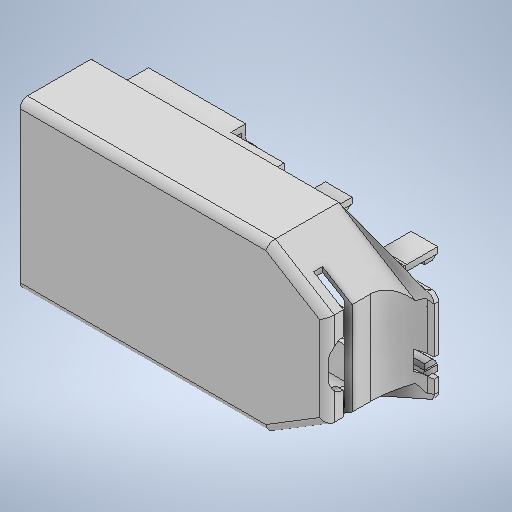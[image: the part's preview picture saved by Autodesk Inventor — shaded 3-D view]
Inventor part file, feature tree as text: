
AUTODESK INVENTOR PART (.ipt)
format: ipt  version: 2025 (Build 290162000, 162)  size: 913,408 bytes
history: native  units: mm
features: extrude x19, reference x11, fillet x7, sketch x5, other x4, plane x3, thicken_offset x2, loft x1, chamfer x1, projected_geometry x1
ambient origin geometry x8: Origin, YZ Plane, XZ Plane, XY Plane, X Axis, Y Axis, Z Axis, Center Point
bodies: Solid1 (feature_tree)
feature tree (54):
  plane  "Work Plane1"
  extrude  "Extrusion1"  Depth=0.4mm
  extrude  "Extrusion2"  Depth=0.4mm
  extrude  "Extrusion3"  Depth=0.5mm
  plane  "Work Plane2"
  loft  "Loft1"
  extrude  "Extrusion4"  Depth=2.0mm TaperAngle=0.0deg
  extrude  "Extrusion5"  Depth=2.0mm
  extrude  "Extrusion6"  Depth=2.0mm
  extrude  "Extrusion7"  Depth=2.0mm
  extrude  "Extrusion8"  Depth=2.0mm
  extrude  "Extrusion9"  Depth=2.0mm
  extrude  "Extrusion10"  TaperAngle=0.0deg  [1 undecoded]
  extrude  "Extrusion11"  TaperAngle=0.0deg  [1 undecoded]
  extrude  "Extrusion12"  Depth=2.0mm TaperAngle=0.0deg
  extrude  "Extrusion13"  Depth=10.0mm TaperAngle=0.0deg
  extrude  "Extrusion14"  Depth=2.0mm TaperAngle=0.0deg
  chamfer  "Chamfer1"  Distance=0.3mm
  thicken_offset  "Thicken1"
  thicken_offset  "Thicken2"
  fillet  "Fillet1"  Radius=0.2mm
  fillet  "Fillet2"  Radius=0.3mm
  fillet  "Fillet3"  Radius=0.3mm
  extrude  "Extrusion15"  Depth=10.0mm TaperAngle=0.0deg
  fillet  "Fillet4"  Radius=0.8mm
  fillet  "Fillet5"  Radius=0.8mm
  fillet  "Fillet6"  Radius=0.4mm
  plane  "Work Plane3"
  extrude  "Extrusion16"  Depth=2.0mm
  extrude  "Extrusion17"  Depth=2.0mm TaperAngle=0.0deg
  fillet  "Fillet7"  Radius=0.5mm
  extrude  "Extrusion18"  Depth=2.0mm
  extrude  "Extrusion20"  Depth=2.0mm
  reference  "Reference5"
  reference  "Reference6"
  reference  "Reference7"
  reference  "Reference8"
  reference  "Reference9"
  reference  "Reference10"
  sketch  "Sketch3"  dims[d0=0.4mm d1=0.4mm]
  other  "Edges1"
  reference  "Reference13"
  reference  "Reference14"
  reference  "Reference15"
  projected_geometry  "Projected Loop1"
  reference  "Reference16"
  reference  "Reference17"
  sketch  "Sketch16"  dims[d2=0.4mm d3=0.4mm]
  sketch  "Sketch19"  dims[d4=0.4mm d5=0.0mm d6=0.5mm]
  sketch  "Sketch20"  dims[d7=0.4mm d8=0.5mm]
  sketch  "Sketch21"  dims[d9=0.3mm d10=0.0mm d11=2.7mm d12=0.0mm d13=0.2mm d14=0.4mm d15=0.5mm d17=4.0mm d18=10.4mm d21=0.0mm d22=90.0deg d23=0.0mm d24=90.0deg d25=2.7mm d26=0.0mm d27=10.0mm d28=0.0mm d29=4.5mm d30=0.0mm d31=0.3mm d32=0.0mm d33=0.2mm d34=0.3mm d35=0.3mm d36=0.0mm d37=10.0mm d38=0.0mm d39=0.8mm d40=0.8mm d41=0.4mm d42=15.5mm d43=0.5mm d44=0.0mm d45=0.5mm d46=0.0mm d47=1.1mm d48=0.6mm d49=9.5mm d50=2.0mm d51=0.0mm d52=0.1mm d53=0.1mm d54=0.2mm d55=0.1mm d56=0.2mm d57=0.2mm d58=0.35mm d59=-0.872665mm d60=0.35mm d61=-0.872665mm d62=0.2mm d63=2.0mm d64=45.0deg d65=0.2mm d66=0.2mm d67=0.2mm d68=0.2mm d69=2.0mm d70=2.0mm d71=0.5mm d72=6.0mm d73=4.0mm d74=1.2mm d75=0.2mm d76=0.0mm d77=0.5mm d78=0.1mm d80=0.1mm d81=0.1mm d82=0.15mm d84=20.777mm d86=-0.4mm d87=0.3mm d88=1.9mm d89=1.5mm d90=0.3mm d91=0.0mm d92=1.575mm d93=1.575mm d94=6.3mm d95=0.9mm d96=1.0mm d97=2.0mm d98=0.0mm d99=0.5mm d100=1.4mm d101=1.3mm d102=2.0mm d103=0.0mm d104=0.9mm d107=0.2mm d108=2.0mm d109=0.0mm]
  parser-record x1  (decoder bookkeeping rows leaked as tree rows — omitted from the tree; the rows remain in map.json)
  other  "np2_full_assembly.iam"
  other  "np2_main_chassis:1"
note: 2 required parameter values undecoded (feature->parameter linkage not recoverable at this tier; creation-order binding heuristic only, values carry confidence <= 0.55)
note: 1 file-system path scrubbed to <path> (originals preserved in map.json)
